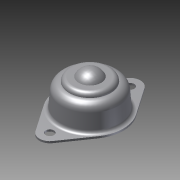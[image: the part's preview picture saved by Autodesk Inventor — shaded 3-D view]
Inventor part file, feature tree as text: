
AUTODESK INVENTOR PART (.ipt)
format: ipt  version: 2011 SP2 (Build 150309200, 309)  size: 146,432 bytes
history: native  units: mm
features: sketch x2, revolve x1, extrude x1
ambient origin geometry x8: Origin, YZ Plane, XZ Plane, XY Plane, X Axis, Y Axis, Z Axis, Center Point
bodies: Solid1 (feature_tree)
feature tree (4):
  revolve  "Revolution1"  [1 undecoded]
  extrude  "Extrusion1"  Depth=34.9mm
  sketch  "Sketch1"  dims[d10=90.0deg d11=4.0mm]
  sketch  "Sketch2"  dims[d12=4.0mm d13=34.9mm d14=19.45mm d15=10.0mm d16=10.0mm d17=32.1mm d18=0.9mm d19=0.0mm]
note: 1 required parameter value undecoded (feature->parameter linkage not recoverable at this tier; creation-order binding heuristic only, values carry confidence <= 0.55)
